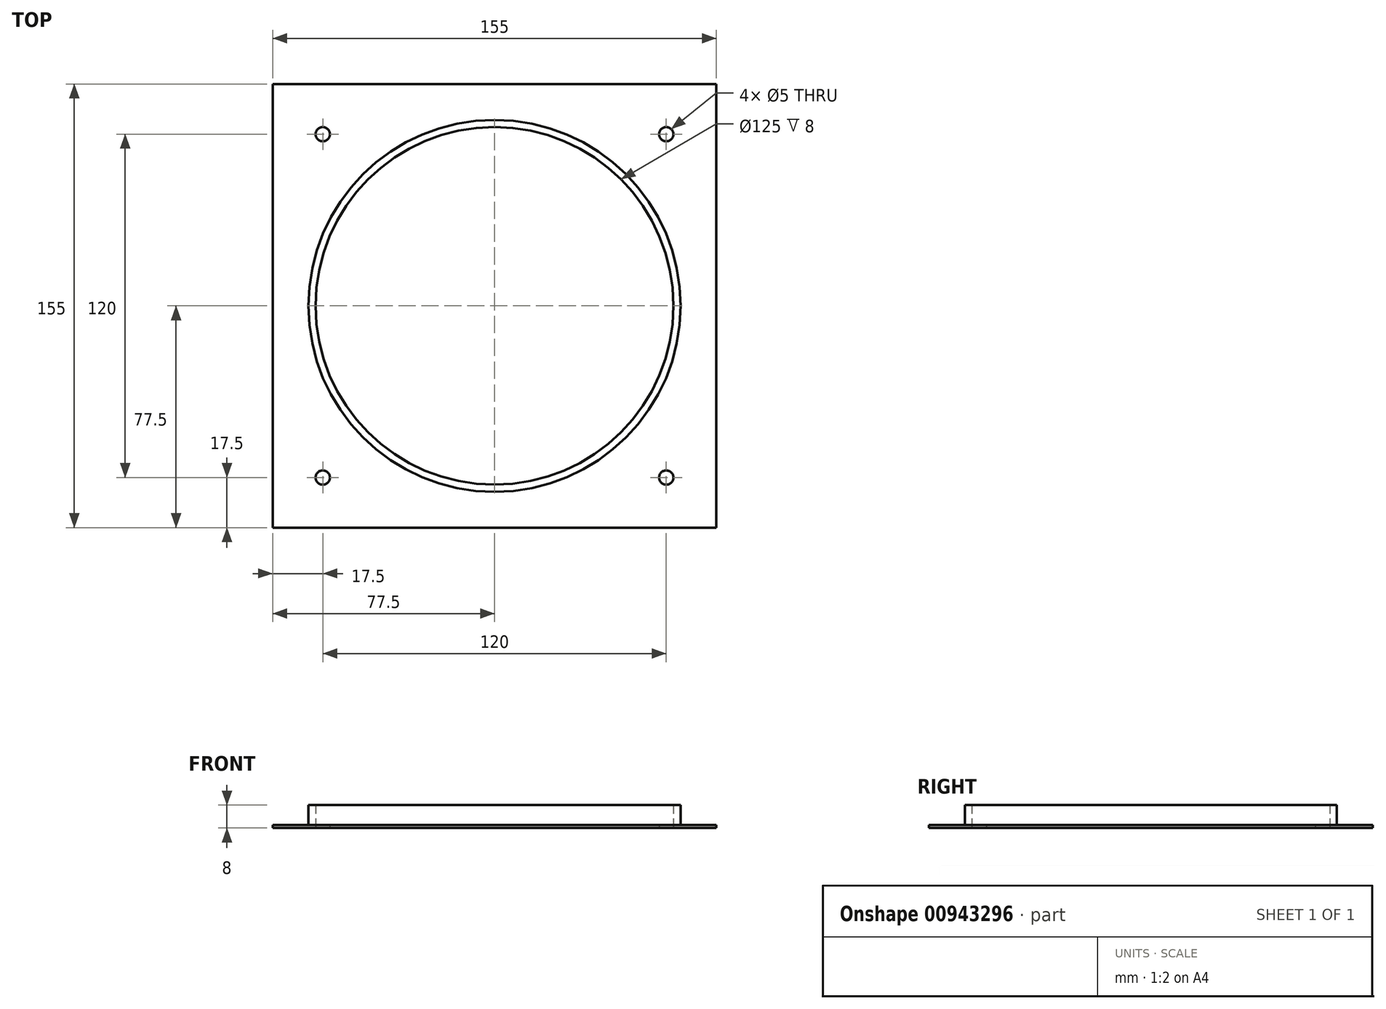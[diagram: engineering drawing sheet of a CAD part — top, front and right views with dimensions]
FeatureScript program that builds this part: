
annotation { "Feature Type Name" : "Feature", "Feature Type Description" : "" }
export const myFeature = defineFeature(function(context is Context, id is Id, definition is map)
    precondition{}
    {
        {
            var Q0;
            Q0=qCreatedBy(makeId("Top.planeOp"),FACE);
            var sketch = newSketch(context, id + "F0", { "sketchPlane" : qUnion([Q0])});
            skLineSegment(sketch, "E0.bottom", {"start": v(77.5, 77.5) * mm, "end": v(-77.5, 77.5) * mm});
            skLineSegment(sketch, "E0.top", {"start": v(77.5, -77.5) * mm, "end": v(-77.5, -77.5) * mm});
            skLineSegment(sketch, "E0.left", {"start": v(77.5, 77.5) * mm, "end": v(77.5, -77.5) * mm});
            skLineSegment(sketch, "E0.right", {"start": v(-77.5, 77.5) * mm, "end": v(-77.5, -77.5) * mm});
            skPoint(sketch, "E0.middle", {"position": v(0, 0) * mm});
            skCircle(sketch, "E1", {"center": v(0, 0) * mm, "radius": 62.5 * mm});
            skLineSegment(sketch, "E2.bottom", {"start": v(60, 60) * mm, "end": v(-60, 60) * mm, "construction": true});
            skLineSegment(sketch, "E2.top", {"start": v(60, -60) * mm, "end": v(-60, -60) * mm, "construction": true});
            skLineSegment(sketch, "E2.left", {"start": v(60, 60) * mm, "end": v(60, -60) * mm, "construction": true});
            skLineSegment(sketch, "E2.right", {"start": v(-60, 60) * mm, "end": v(-60, -60) * mm, "construction": true});
            skCircle(sketch, "E3", {"center": v(-60, 60) * mm, "radius": 2.5 * mm});
            skCircle(sketch, "E4", {"center": v(60, 60) * mm, "radius": 2.5 * mm});
            skCircle(sketch, "E5", {"center": v(60, -60) * mm, "radius": 2.5 * mm});
            skCircle(sketch, "E6", {"center": v(-60, -60) * mm, "radius": 2.5 * mm});
            skSolve(sketch);
        }
        {
            var Q0;
            Q0 = qSketchRegion(id + "F0", true);
            extrude(context, id + "F1", {"entities" : qUnion([Q0]), "depth" : 1 * mm, "offsetDistance" : 25 * mm});
        }
        {
            var Q0;
            Q0=makeQuery(id+"F1.opExtrude","CAP_FACE",FACE,{"disambiguationData":[OSD([sQuery(id+"F0.wireOp",EDGE,"E0.bottom"),sQuery(id+"F0.wireOp",EDGE,"E0.top"),sQuery(id+"F0.wireOp",EDGE,"E0.left"),sQuery(id+"F0.wireOp",EDGE,"E0.right"),sQuery(id+"F0.wireOp",EDGE,"E1"),sQuery(id+"F0.wireOp",EDGE,"E3"),sQuery(id+"F0.wireOp",EDGE,"E4"),sQuery(id+"F0.wireOp",EDGE,"E5"),sQuery(id+"F0.wireOp",EDGE,"E6")])],"isStart":false});
            var sketch = newSketch(context, id + "F2", { "sketchPlane" : qUnion([Q0])});
            skCircle(sketch, "E7", {"center": v(0, 0) * mm, "radius": 62.5 * mm});
            skCircle(sketch, "E8", {"center": v(0, 0) * mm, "radius": 65 * mm});
            skSolve(sketch);
        }
        {
            var Q0;
            Q0 = qSketchRegion(id + "F2", true);
            extrude(context, id + "F3", {"entities" : qUnion([Q0]), "operationType" : NewBodyOperationType.ADD, "depth" : 7 * mm, "offsetDistance" : 25 * mm});
        }
    });
